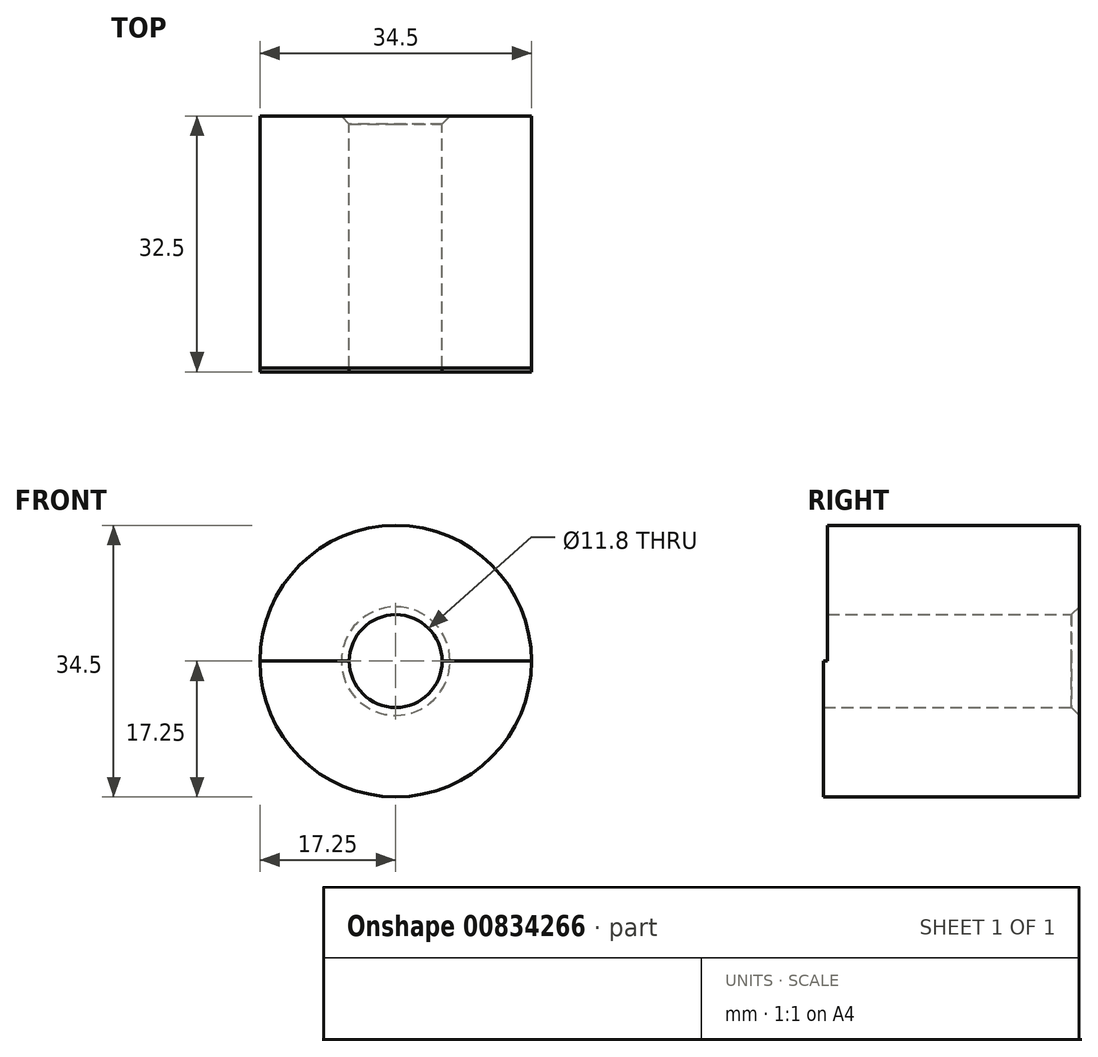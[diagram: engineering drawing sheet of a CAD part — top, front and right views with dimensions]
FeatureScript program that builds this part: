
annotation { "Feature Type Name" : "Feature", "Feature Type Description" : "" }
export const myFeature = defineFeature(function(context is Context, id is Id, definition is map)
    precondition{}
    {
        {
            var Q0;
            Q0=qCreatedBy(makeId("Front.planeOp"),FACE);
            var sketch = newSketch(context, id + "F0", { "sketchPlane" : qUnion([Q0])});
            skCircle(sketch, "E0", {"center": v(0, 0) * mm, "radius": 17.25 * mm});
            skCircle(sketch, "E1", {"center": v(0, 0) * mm, "radius": 5.9 * mm});
            skSolve(sketch);
        }
        {
            var Q0;
            Q0=makeQuery(id+"F0.imprint","IMPRINT",FACE,{"disambiguationData":[TD([[makeQuery(id+"F0.imprint","IMPRINT",EDGE,{"derivedFrom":sQuery(id+"F0.wireOp",EDGE,"E0")}),1.0]])]});
            extrude(context, id + "F1", {"entities" : qUnion([Q0]), "depth" : 32.5 * mm, "offsetDistance" : 25 * mm});
        }
        {
            var Q0;
            Q0=makeQuery(id+"F1.opExtrude","CAP_FACE",FACE,{"disambiguationData":[OSD([sQuery(id+"F0.wireOp",EDGE,"E0"),sQuery(id+"F0.wireOp",EDGE,"E1")])],"isStart":false});
            var sketch = newSketch(context, id + "F2", { "sketchPlane" : qUnion([Q0])});
            skLineSegment(sketch, "E2", {"start": v(-17.25, 0) * mm, "end": v(17.25, 0) * mm});
            skSolve(sketch);
        }
        {
            var Q0;
            {var subQ0=sQuery(id+"F2.wireOp",EDGE,"E2");var subQ1=makeQuery(id+"F1.opExtrude","CAP_EDGE",EDGE,{"disambiguationData":[OSD([sQuery(id+"F0.wireOp",EDGE,"E0")])],"isStart":false});var subQ2=makeQuery(id+"F2.imprint","INTERSECT",VERTEX,{"disambiguationData":[OD(0.0)],"derivedFrom":[subQ1,subQ0]});Q0=makeQuery(id+"F2.imprint","IMPRINT",FACE,{"disambiguationData":[TD([[makeQuery(id+"F2.imprint","IMPRINT",EDGE,{"disambiguationData":[TD([[subQ2,-1.0]])],"derivedFrom":subQ0}),1.0]])]});}
            extrude(context, id + "F3", {"entities" : qUnion([Q0]), "operationType" : NewBodyOperationType.REMOVE, "oppositeDirection" : true, "depth" : .5 * mm, "offsetDistance" : 25 * mm});
        }
        {
            var Q0;
            Q0=makeQuery(id+"F1.opExtrude","CAP_EDGE",EDGE,{"disambiguationData":[OSD([sQuery(id+"F0.wireOp",EDGE,"E1")])],"isStart":true});
            chamfer(context, id + "F4", {"entities" : qUnion([Q0]), "width" : 1 * mm, "tangentPropagation" : true});
        }
    });
